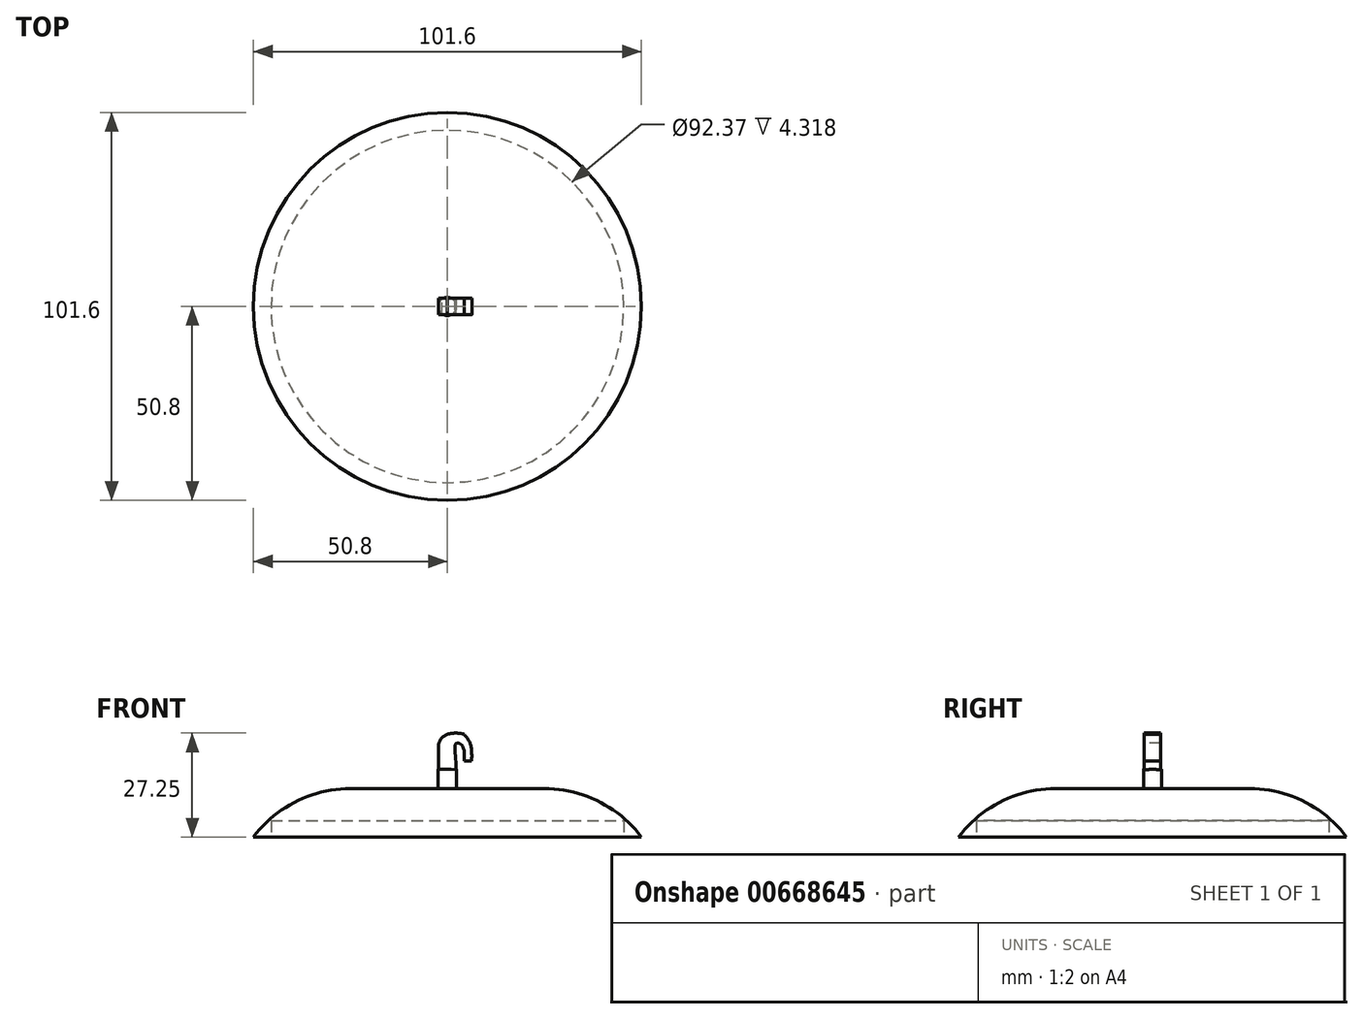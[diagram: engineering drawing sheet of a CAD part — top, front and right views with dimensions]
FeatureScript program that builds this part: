
annotation { "Feature Type Name" : "Feature", "Feature Type Description" : "" }
export const myFeature = defineFeature(function(context is Context, id is Id, definition is map)
    precondition{}
    {
        {
            var Q0;
            Q0=qCreatedBy(makeId("Top.planeOp"),FACE);
            var sketch = newSketch(context, id + "F0", { "sketchPlane" : qUnion([Q0])});
            skCircle(sketch, "E0", {"center": v(0, 0) * mm, "radius": 50.8 * mm});
            skSolve(sketch);
        }
        {
            var Q0;
            Q0 = qSketchRegion(id + "F0", true);
            extrude(context, id + "F1", {"entities" : qUnion([Q0]), "depth" : 12.7 * mm, "offsetDistance" : 25.4 * mm});
        }
        {
            var Q0;
            Q0=makeQuery(id+"F1.opExtrude","CAP_FACE",FACE,{"disambiguationData":[OSD([sQuery(id+"F0.wireOp",EDGE,"E0")])],"isStart":false});
            fillet(context, id + "F2", {"entities" : qUnion([Q0]), "radius" : 31.75 * mm, "tangentPropagation" : true, "allowEdgeOverflow" : false});
        }
        {
            var Q0;
            Q0=makeQuery(id+"F1.opExtrude","CAP_FACE",FACE,{"disambiguationData":[OSD([sQuery(id+"F0.wireOp",EDGE,"E0")])],"isStart":false});
            var sketch = newSketch(context, id + "F3", { "sketchPlane" : qUnion([Q0])});
            skSolve(sketch);
        }
        {
            var Q0;
            {var subQ0=sQuery(id+"F0.wireOp",EDGE,"E0");Q0=makeQuery(id+"F3.imprint","IMPRINT",FACE,{"disambiguationData":[TD([[makeQuery(id+"F3.imprint","IMPRINT",EDGE,{"derivedFrom":makeQuery(id+"F2.opFillet","BLEND_EDGE",EDGE,{"blendedFrom":[makeQuery(id+"F1.opExtrude","CAP_EDGE",EDGE,{"disambiguationData":[OSD([subQ0])],"isStart":false}),makeQuery(id+"F1.opExtrude","CAP_FACE",FACE,{"disambiguationData":[OSD([subQ0])],"isStart":false})],"blendedInto":[makeQuery(id+"F1.opExtrude","CAP_FACE",FACE,{"disambiguationData":[OSD([subQ0])],"isStart":false})]})}),1.0]])]});}
            var sketch = newSketch(context, id + "F4", { "sketchPlane" : qUnion([Q0])});
            skCircle(sketch, "E1", {"center": v(0, 0) * mm, "radius": 2.38 * mm});
            skSolve(sketch);
        }
        {
            var Q0;
            Q0 = qSketchRegion(id + "F4", true);
            extrude(context, id + "F5", {"entities" : qUnion([Q0]), "operationType" : NewBodyOperationType.ADD, "depth" : 5.08 * mm, "offsetDistance" : 25.4 * mm});
        }
        {
            var Q0;
            Q0=qCreatedBy(makeId("Front.planeOp"),FACE);
            var sketch = newSketch(context, id + "F6", { "sketchPlane" : qUnion([Q0])});
            skLineSegment(sketch, "E2", {"start": v(-2.33, 17.8) * mm, "end": v(-2.33, 23.8) * mm});
            skArc(sketch, "E3", {"start": v(0, 26.9) * mm, "mid": v(-1.69, 25.74) * mm, "end": v(-2.33, 23.8) * mm});
            skArc(sketch, "E4", {"start": v(4.4, 26.9) * mm, "mid": v(2.2, 27.25) * mm, "end": v(0, 26.9) * mm});
            skFitSpline(sketch, "E5", {"points": [v(4.4, 26.9) * mm, v(6, 24.45) * mm, v(6.36, 19.89) * mm], "startDerivative": vector(4.27, -4.92) * mm, "endDerivative": vector(-0.18, -8.96) * mm});
            skLineSegment(sketch, "E6", {"start": v(6.36, 19.89) * mm, "end": v(4.35, 19.89) * mm});
            skPoint(sketch, "E7.3.internal.snap0", {"position": v(2.2, 27.25) * mm});
            skFitSpline(sketch, "E7", {"points": [v(4.35, 19.89) * mm, v(4.35, 22.76) * mm, v(3.38, 24.45) * mm, v(2.2, 24.45) * mm, v(2.2, 20.07) * mm, v(2.2, 17.7) * mm], "startDerivative": vector(1.2, 13.83) * mm, "endDerivative": vector(-0.72, -9.88) * mm});
            skLineSegment(sketch, "E8", {"start": v(-2.33, 17.8) * mm, "end": v(2.2, 17.7) * mm});
            skSolve(sketch);
        }
        {
            var Q0;
            Q0 = qSketchRegion(id + "F6", true);
            var Q1;
            Q1=makeQuery(id+"F6.imprint","IMPRINT",FACE,{"disambiguationData":[TD([[makeQuery(id+"F6.imprint","IMPRINT",EDGE,{"derivedFrom":sQuery(id+"F6.wireOp",EDGE,"E2")}),-1.0]])]});
            extrude(context, id + "F7", {"entities" : qUnion([Q0, Q1]), "operationType" : NewBodyOperationType.ADD, "depth" : 4.32 * mm, "offsetDistance" : 25.4 * mm, "symmetric" : true});
        }
        {
            var Q0;
            Q0=makeQuery(id+"F1.opExtrude","CAP_FACE",FACE,{"disambiguationData":[OSD([sQuery(id+"F0.wireOp",EDGE,"E0")])],"isStart":true});
            var sketch = newSketch(context, id + "F8", { "sketchPlane" : qUnion([Q0])});
            skCircle(sketch, "E9", {"center": v(0, 0) * mm, "radius": 46.18 * mm});
            skSolve(sketch);
        }
        {
            var Q0;
            Q0=makeQuery(id+"F8.imprint","IMPRINT",FACE,{"disambiguationData":[TD([[makeQuery(id+"F8.imprint","IMPRINT",EDGE,{"derivedFrom":sQuery(id+"F8.wireOp",EDGE,"E9")}),1.0]])]});
            extrude(context, id + "F9", {"entities" : qUnion([Q0]), "operationType" : NewBodyOperationType.REMOVE, "oppositeDirection" : true, "depth" : 4.32 * mm, "offsetDistance" : 25.4 * mm});
        }
    });
